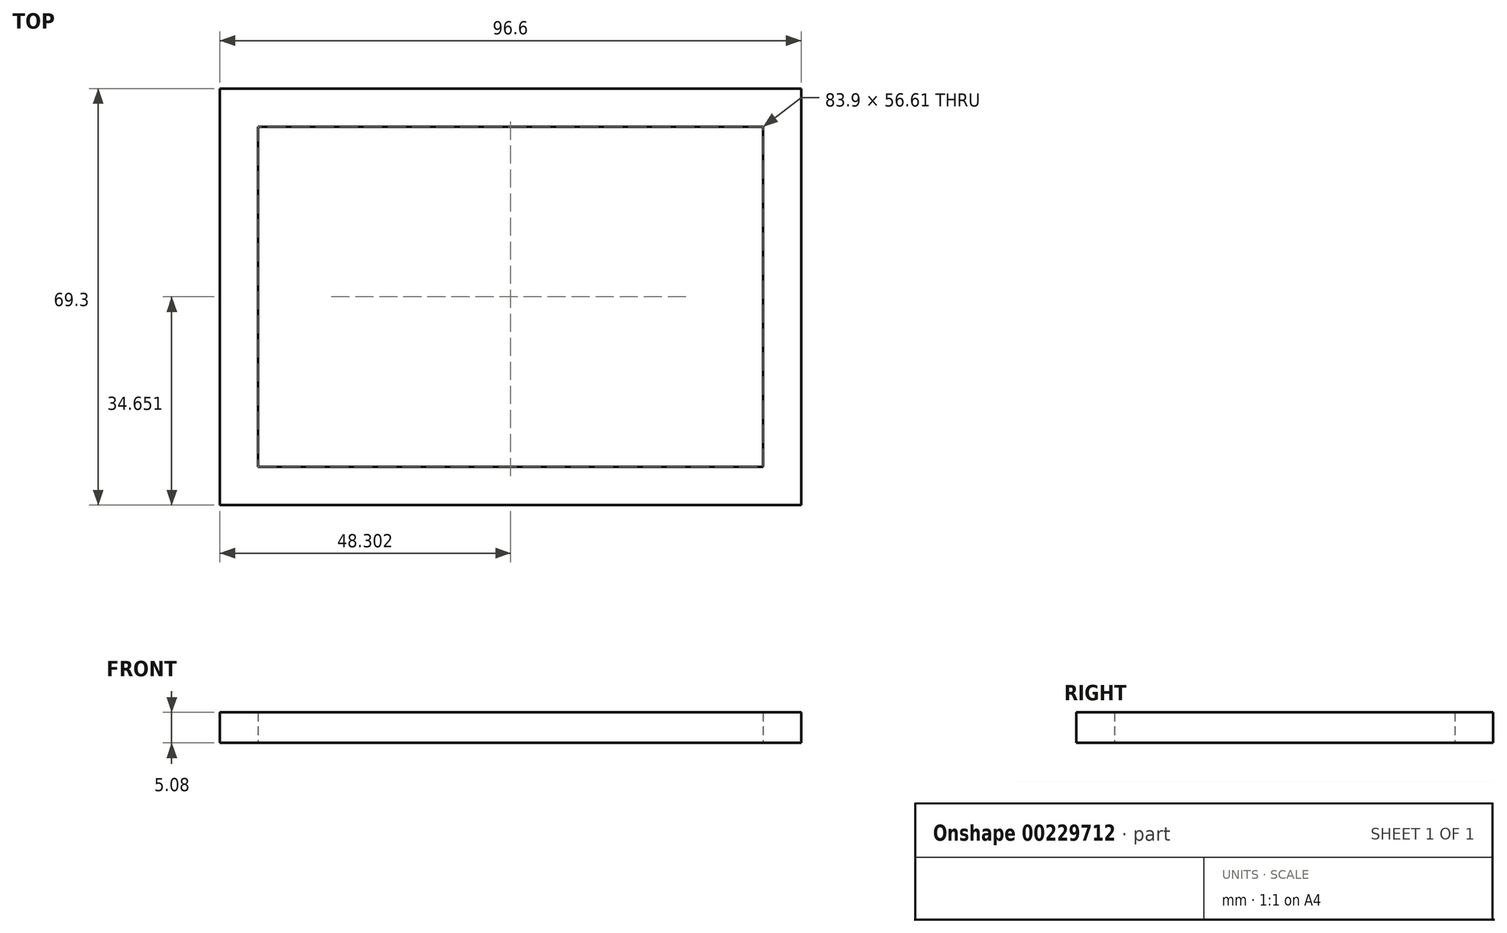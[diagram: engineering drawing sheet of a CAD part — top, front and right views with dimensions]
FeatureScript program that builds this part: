
annotation { "Feature Type Name" : "Feature", "Feature Type Description" : "" }
export const myFeature = defineFeature(function(context is Context, id is Id, definition is map)
    precondition{}
    {
        {
            var Q0;
            Q0=qCreatedBy(makeId("Top.planeOp"),FACE);
            var sketch = newSketch(context, id + "F0", { "sketchPlane" : qUnion([Q0])});
            skLineSegment(sketch, "E0.bottom", {"start": v(-46.63, 30.32) * mm, "end": v(49.97, 30.32) * mm});
            skLineSegment(sketch, "E0.top", {"start": v(-46.63, -38.98) * mm, "end": v(49.97, -38.98) * mm});
            skLineSegment(sketch, "E0.left", {"start": v(-46.63, 30.32) * mm, "end": v(-46.63, -38.98) * mm});
            skLineSegment(sketch, "E0.right", {"start": v(49.97, 30.32) * mm, "end": v(49.97, -38.98) * mm});
            skLineSegment(sketch, "E1.0", {"start": v(-40.28, -32.63) * mm, "end": v(43.62, -32.63) * mm});
            skLineSegment(sketch, "E1.1", {"start": v(-40.28, 23.97) * mm, "end": v(-40.28, -32.63) * mm});
            skLineSegment(sketch, "E1.2", {"start": v(-40.28, 23.97) * mm, "end": v(43.62, 23.97) * mm});
            skLineSegment(sketch, "E1.3", {"start": v(43.62, 23.97) * mm, "end": v(43.62, -32.63) * mm});
            skSolve(sketch);
        }
        {
            var Q0;
            Q0=makeQuery(id+"F0.imprint","IMPRINT",FACE,{"disambiguationData":[TD([[makeQuery(id+"F0.imprint","IMPRINT",EDGE,{"derivedFrom":sQuery(id+"F0.wireOp",EDGE,"E0.bottom")}),-1.0]])]});
            var Q1;
            Q1 = qConstructionFilter(qBodyType(qCreatedBy(id + "F0" ,EDGE), BodyType.WIRE), ConstructionObject.NO);
            extrude(context, id + "F1", {"entities" : qUnion([Q0]), "surfaceEntities" : qUnion([Q1]), "depth" : 5.08 * mm});
        }
    });
